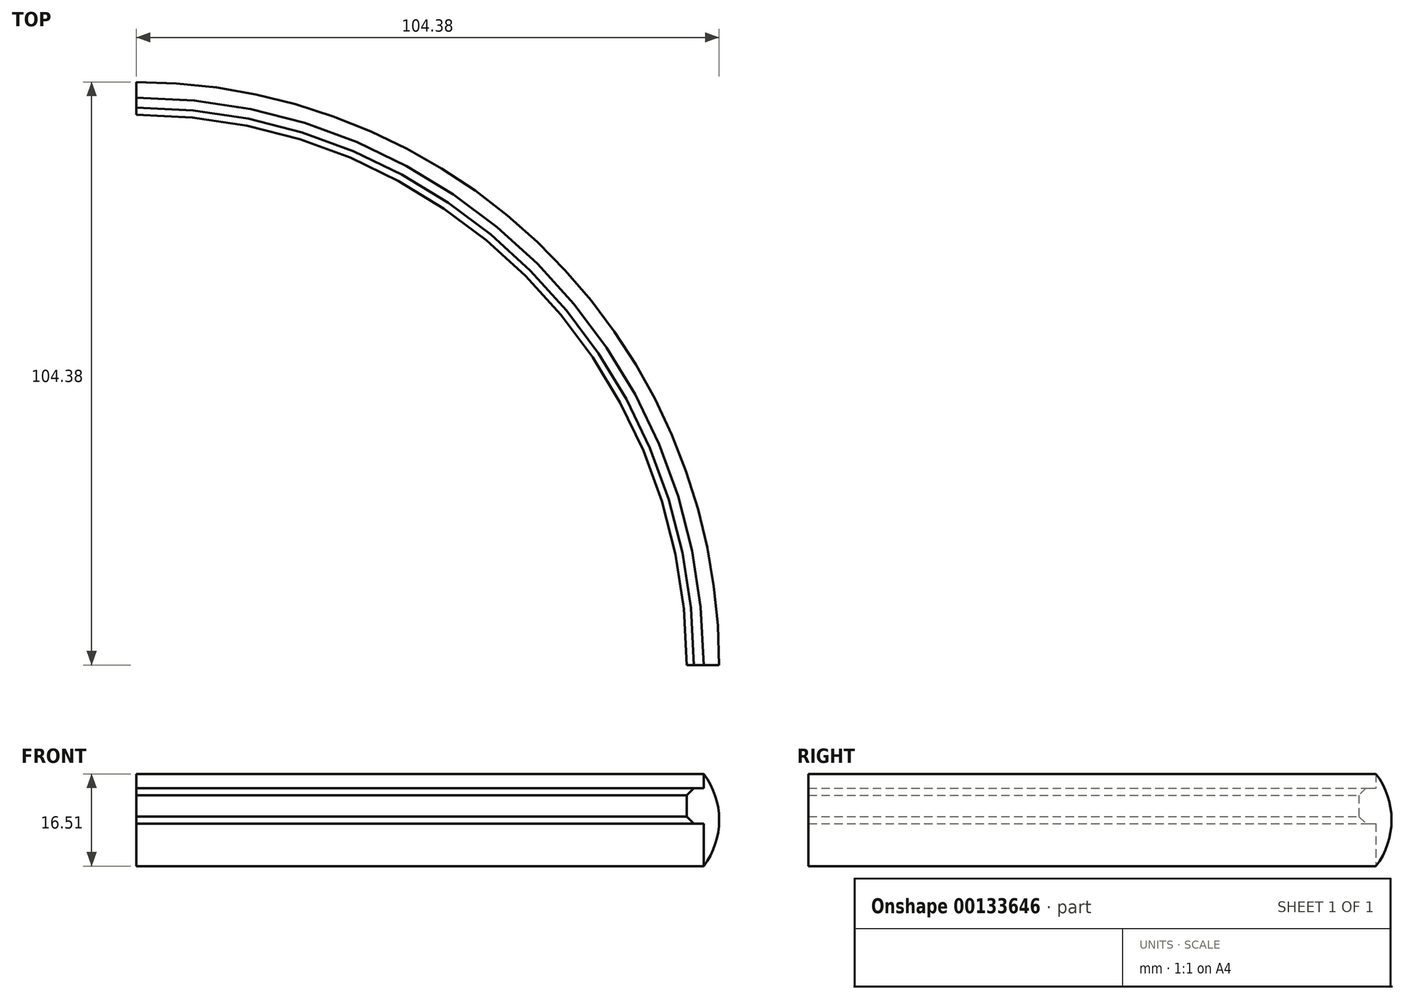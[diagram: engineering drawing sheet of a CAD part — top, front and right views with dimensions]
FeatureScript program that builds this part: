
annotation { "Feature Type Name" : "Feature", "Feature Type Description" : "" }
export const myFeature = defineFeature(function(context is Context, id is Id, definition is map)
    precondition{}
    {
        {
            var Q0;
            Q0=qCreatedBy(makeId("Top.planeOp"),FACE);
            var sketch = newSketch(context, id + "F0", { "sketchPlane" : qUnion([Q0])});
            skArc(sketch, "E0", {"start": v(101.6, 0) * mm, "mid": v(71.84, 71.84) * mm, "end": v(0, 101.6) * mm});
            skArc(sketch, "E1.0", {"start": v(98.55, 0) * mm, "mid": v(69.69, 69.69) * mm, "end": v(0, 98.55) * mm});
            skLineSegment(sketch, "E2", {"start": v(0, 98.55) * mm, "end": v(0, 101.6) * mm});
            skLineSegment(sketch, "E3", {"start": v(98.55, 0) * mm, "end": v(101.6, 0) * mm});
            skSolve(sketch);
        }
        {
            var Q0;
            Q0=makeQuery(id+"F0.imprint","IMPRINT",FACE,{"disambiguationData":[TD([[makeQuery(id+"F0.imprint","IMPRINT",EDGE,{"derivedFrom":sQuery(id+"F0.wireOp",EDGE,"E0")}),1.0]])]});
            extrude(context, id + "F1", {"entities" : qUnion([Q0]), "depth" : 6.35 * mm});
        }
        {
            var Q0;
            Q0=makeQuery(id+"F1.opExtrude","SWEPT_FACE",FACE,{"disambiguationData":[OSD([sQuery(id+"F0.wireOp",EDGE,"E3")])]});
            var sketch = newSketch(context, id + "F2", { "sketchPlane" : qUnion([Q0])});
            skLineSegment(sketch, "E4", {"start": v(101.6, 3.18) * mm, "end": v(104.14, 3.18) * mm});
            skLineSegment(sketch, "E5", {"start": v(101.6, 0) * mm, "end": v(101.6, -7.62) * mm});
            skLineSegment(sketch, "E6", {"start": v(101.6, 6.35) * mm, "end": v(101.6, 8.9) * mm});
            skLineSegment(sketch, "E7", {"start": v(101.6, 0) * mm, "end": v(101.6, 6.35) * mm});
            skArc(sketch, "E8", {"start": v(101.6, -7.62) * mm, "mid": v(104.38, 0.64) * mm, "end": v(101.6, 8.9) * mm});
            skSolve(sketch);
        }
        {
            var Q0;
            Q0=qCreatedBy(makeId("Front.planeOp"),FACE);
            var sketch = newSketch(context, id + "F3", { "sketchPlane" : qUnion([Q0])});
            skLineSegment(sketch, "E9", {"start": v(0, 0) * mm, "end": v(0, 60.52) * mm});
            skSolve(sketch);
        }
        {
            var Q0;
            {var subQ0=sQuery(id+"F2.wireOp",EDGE,"E4");Q0=makeQuery(id+"F2.imprint","IMPRINT",FACE,{"disambiguationData":[TD([[makeQuery(id+"F2.imprint","IMPRINT",EDGE,{"derivedFrom":subQ0}),-1.0]])]});}
            var Q1;
            {var subQ0=sQuery(id+"F2.wireOp",EDGE,"E4");Q1=makeQuery(id+"F2.imprint","IMPRINT",FACE,{"disambiguationData":[TD([[makeQuery(id+"F2.imprint","IMPRINT",EDGE,{"derivedFrom":subQ0}),1.0]])]});}
            var Q2;
            Q2=sQuery(id+"F3.wireOp",EDGE,"E9");
            revolve(context, id + "F4", {"operationType" : NewBodyOperationType.ADD, "entities" : qUnion([Q0, Q1]), "axis" : qUnion([Q2]), "revolveType" : RevolveType.ONE_DIRECTION, "angle" : 90 * degree});
        }
        {
            var Q0;
            Q0=makeQuery(id+"F1.opExtrude","CAP_EDGE",EDGE,{"disambiguationData":[OSD([sQuery(id+"F0.wireOp",EDGE,"E1.0")])],"isStart":true});
            chamfer(context, id + "F5", {"entities" : qUnion([Q0]), "width" : 1.27 * mm, "tangentPropagation" : true});
        }
        {
            var Q0;
            Q0=makeQuery(id+"F1.opExtrude","CAP_EDGE",EDGE,{"disambiguationData":[OSD([sQuery(id+"F0.wireOp",EDGE,"E1.0")])],"isStart":false});
            chamfer(context, id + "F6", {"entities" : qUnion([Q0]), "width" : 1.27 * mm, "tangentPropagation" : true});
        }
    });
